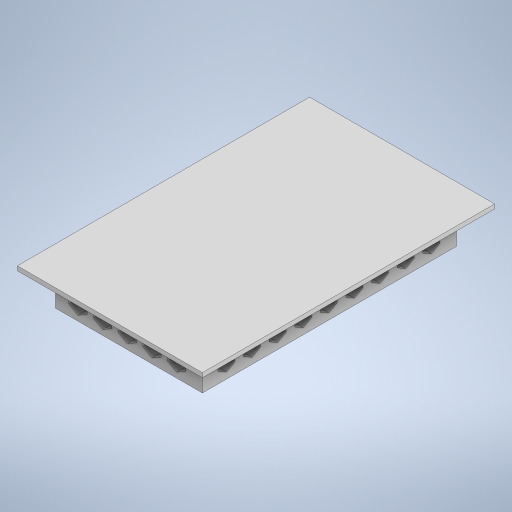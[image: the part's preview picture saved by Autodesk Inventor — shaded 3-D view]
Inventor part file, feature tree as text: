
AUTODESK INVENTOR PART (.ipt)
format: ipt  version: 2023 (Build 270158000, 158)  size: 944,640 bytes
history: native  units: mm
features: extrude x10, sketch x9, shell x1
ambient origin geometry x8: Origin, YZ Plane, XZ Plane, XY Plane, X Axis, Y Axis, Z Axis, Center Point
bodies: Solid1 (feature_tree)
feature tree (20):
  sketch  "Sketch1"  dims[d0=77.5mm d1=134.0mm]
  extrude  "Extrusion1"  Depth=134.0mm
  extrude  "Extrusion2"  Depth=5.0mm
  shell  "Shell1"  Thickness=5.0mm
  extrude  "Extrusion3"  Depth=3.0mm TaperAngle=0.0deg
  extrude  "Extrusion4"  Depth=4.0mm
  extrude  "Extrusion5"  Depth=4.0mm
  extrude  "Extrusion6"  Depth=8.0mm
  extrude  "Extrusion7"  Depth=4.0mm TaperAngle=0.0deg
  extrude  "Extrusion8"  Depth=0.3mm TaperAngle=0.0deg
  extrude  "Extrusion9"  Depth=5.0mm
  extrude  "Extrusion10"  Depth=5.0mm
  sketch  "Sketch2"  dims[d2=5.0mm d3=5.0mm d4=5.0mm]
  sketch  "Sketch3"  dims[d5=5.0mm d6=3.0mm d7=0.0mm]
  sketch  "Sketch4"  dims[d8=2.0mm d9=0.0mm d10=4.0mm]
  sketch  "Sketch5"  dims[d11=1.0mm d12=0.0mm d13=4.0mm]
  sketch  "Sketch6"  dims[d14=1.0mm d15=8.0mm]
  sketch  "Sketch7"  dims[d16=100.0mm d18=12.0mm d19=60.0mm d21=12.0mm d24=4.0mm d25=0.0mm]
  sketch  "Sketch8"  dims[d26=4.0mm d27=0.0mm d28=0.3mm d29=0.0mm]
  sketch  "Sketch9"  dims[d30=10.0mm d31=0.0mm d32=5.0mm d33=5.0mm d34=5.0mm d35=5.0mm d36=2.3mm d37=0.0mm d38=90.0mm d40=13.5mm d41=10.0mm d43=10.0mm d45=222.0mm d46=0.0mm d47=50.0mm d49=13.0mm d50=10.0mm d52=10.0mm d54=222.0mm d55=0.0mm]
